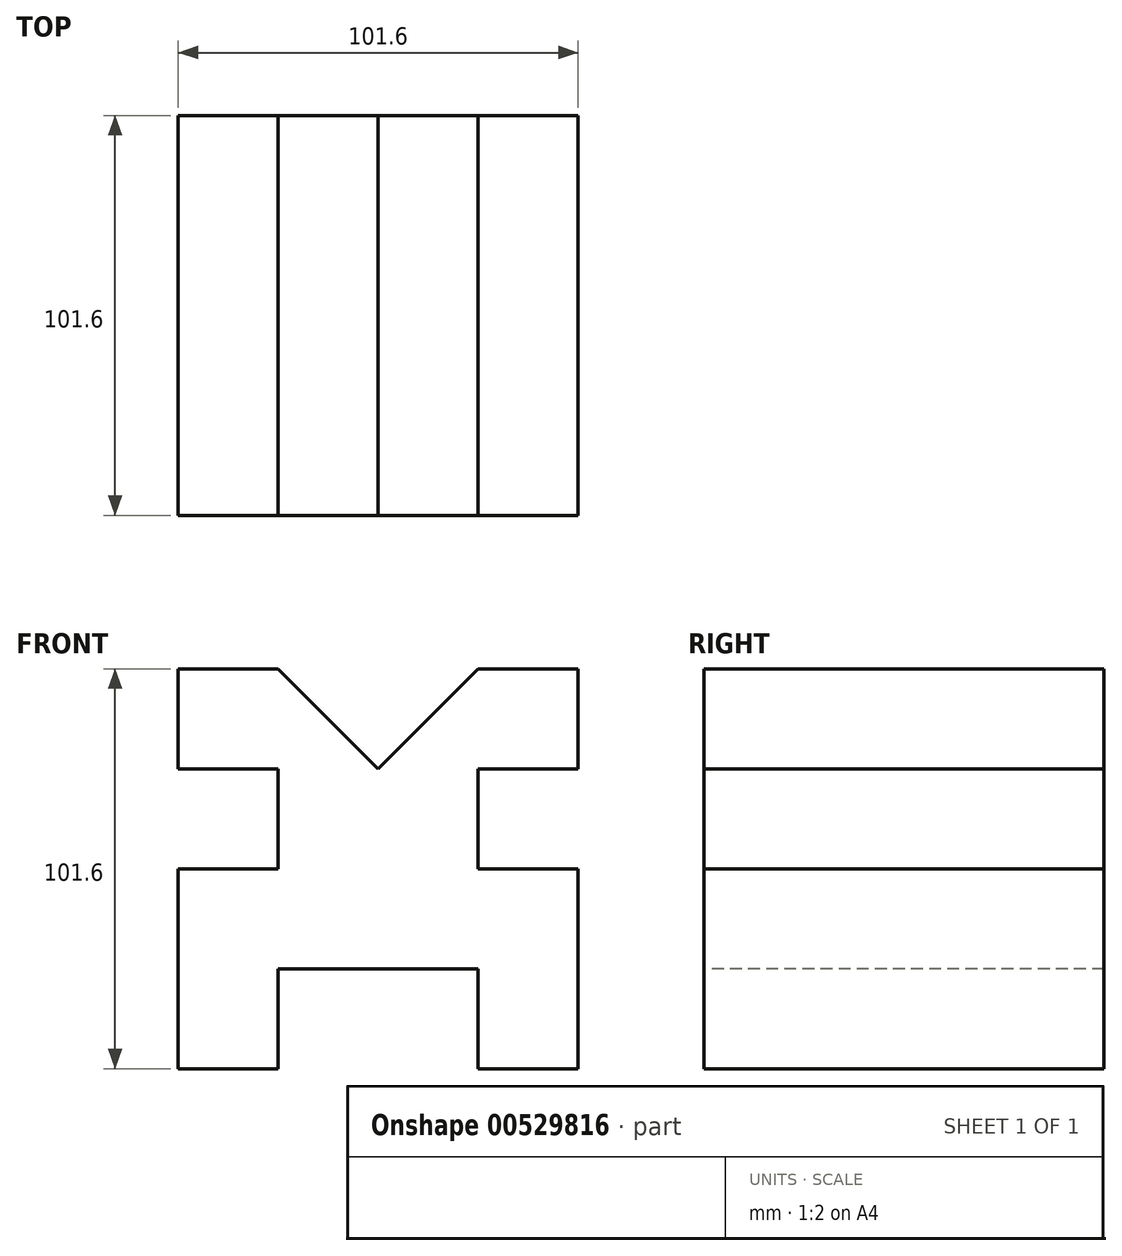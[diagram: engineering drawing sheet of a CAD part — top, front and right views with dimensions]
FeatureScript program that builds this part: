
annotation { "Feature Type Name" : "Feature", "Feature Type Description" : "" }
export const myFeature = defineFeature(function(context is Context, id is Id, definition is map)
    precondition{}
    {
        {
            var Q0;
            Q0=qCreatedBy(makeId("Front.planeOp"),FACE);
            var sketch = newSketch(context, id + "F0", { "sketchPlane" : qUnion([Q0])});
            skLineSegment(sketch, "E0.bottom", {"start": v(-154.32, -86.43) * mm, "end": v(-52.72, -86.43) * mm});
            skLineSegment(sketch, "E0.top", {"start": v(-154.32, 15.17) * mm, "end": v(-52.72, 15.17) * mm});
            skLineSegment(sketch, "E0.left", {"start": v(-154.32, -86.43) * mm, "end": v(-154.32, 15.17) * mm});
            skLineSegment(sketch, "E0.right", {"start": v(-52.72, -86.43) * mm, "end": v(-52.72, 15.17) * mm});
            skSolve(sketch);
        }
        {
            var Q0;
            Q0=makeQuery(id+"F0.imprint","IMPRINT",FACE,{"disambiguationData":[TD([[makeQuery(id+"F0.imprint","IMPRINT",EDGE,{"derivedFrom":sQuery(id+"F0.wireOp",EDGE,"E0.bottom")}),1.0]])]});
            extrude(context, id + "F1", {"entities" : qUnion([Q0]), "depth" : 101.6 * mm, "offsetDistance" : 25.4 * mm});
        }
        {
            var Q0;
            Q0=makeQuery(id+"F1.opExtrude","CAP_FACE",FACE,{"disambiguationData":[OSD([sQuery(id+"F0.wireOp",EDGE,"E0.bottom"),sQuery(id+"F0.wireOp",EDGE,"E0.top"),sQuery(id+"F0.wireOp",EDGE,"E0.left"),sQuery(id+"F0.wireOp",EDGE,"E0.right")])],"isStart":false});
            var sketch = newSketch(context, id + "F2", { "sketchPlane" : qUnion([Q0])});
            skLineSegment(sketch, "E1.bottom", {"start": v(-154.32, 15.17) * mm, "end": v(-128.92, 15.17) * mm});
            skLineSegment(sketch, "E1.top", {"start": v(-154.32, -10.23) * mm, "end": v(-128.92, -10.23) * mm});
            skLineSegment(sketch, "E1.left", {"start": v(-154.32, 15.17) * mm, "end": v(-154.32, -10.23) * mm});
            skLineSegment(sketch, "E1.right", {"start": v(-128.92, 15.17) * mm, "end": v(-128.92, -10.23) * mm});
            skLineSegment(sketch, "E2.bottom", {"start": v(-154.32, -86.43) * mm, "end": v(-128.92, -86.43) * mm});
            skLineSegment(sketch, "E2.top", {"start": v(-154.32, -35.63) * mm, "end": v(-128.92, -35.63) * mm});
            skLineSegment(sketch, "E2.left", {"start": v(-154.32, -86.43) * mm, "end": v(-154.32, -35.63) * mm});
            skLineSegment(sketch, "E2.right", {"start": v(-128.92, -86.43) * mm, "end": v(-128.92, -35.63) * mm});
            skLineSegment(sketch, "E3", {"start": v(-128.92, -35.63) * mm, "end": v(-128.92, -10.23) * mm});
            skLineSegment(sketch, "E4.bottom", {"start": v(-52.72, 15.17) * mm, "end": v(-78.12, 15.17) * mm});
            skLineSegment(sketch, "E4.top", {"start": v(-52.72, -10.23) * mm, "end": v(-78.12, -10.23) * mm});
            skLineSegment(sketch, "E4.left", {"start": v(-52.72, 15.17) * mm, "end": v(-52.72, -10.23) * mm});
            skLineSegment(sketch, "E4.right", {"start": v(-78.12, 15.17) * mm, "end": v(-78.12, -10.23) * mm});
            skLineSegment(sketch, "E5.bottom", {"start": v(-52.72, -86.43) * mm, "end": v(-78.12, -86.43) * mm});
            skLineSegment(sketch, "E5.top", {"start": v(-52.72, -35.63) * mm, "end": v(-78.12, -35.63) * mm});
            skLineSegment(sketch, "E5.left", {"start": v(-52.72, -86.43) * mm, "end": v(-52.72, -35.63) * mm});
            skLineSegment(sketch, "E5.right", {"start": v(-78.12, -86.43) * mm, "end": v(-78.12, -35.63) * mm});
            skLineSegment(sketch, "E6", {"start": v(-78.12, -10.23) * mm, "end": v(-78.12, -35.63) * mm});
            skSolve(sketch);
        }
        {
            var Q0;
            {var subQ0=sQuery(id+"F2.wireOp",EDGE,"E4.top");Q0=makeQuery(id+"F2.imprint","IMPRINT",FACE,{"disambiguationData":[TD([[makeQuery(id+"F2.imprint","IMPRINT",EDGE,{"derivedFrom":subQ0}),1.0]])]});}
            var Q1;
            {var subQ0=sQuery(id+"F2.wireOp",EDGE,"E1.top");Q1=makeQuery(id+"F2.imprint","IMPRINT",FACE,{"disambiguationData":[TD([[makeQuery(id+"F2.imprint","IMPRINT",EDGE,{"derivedFrom":subQ0}),-1.0]])]});}
            extrude(context, id + "F3", {"entities" : qUnion([Q0, Q1]), "operationType" : NewBodyOperationType.REMOVE, "oppositeDirection" : true, "depth" : 101.6 * mm, "offsetDistance" : 25.4 * mm});
        }
        {
            var Q0;
            Q0=makeQuery(id+"F1.opExtrude","CAP_FACE",FACE,{"disambiguationData":[OSD([sQuery(id+"F0.wireOp",EDGE,"E0.bottom"),sQuery(id+"F0.wireOp",EDGE,"E0.top"),sQuery(id+"F0.wireOp",EDGE,"E0.left"),sQuery(id+"F0.wireOp",EDGE,"E0.right")])],"isStart":false});
            var sketch = newSketch(context, id + "F4", { "sketchPlane" : qUnion([Q0])});
            skLineSegment(sketch, "E7", {"start": v(-128.92, -10.23) * mm, "end": v(-78.12, -10.23) * mm});
            skLineSegment(sketch, "E8", {"start": v(-128.92, 15.17) * mm, "end": v(-103.52, -10.23) * mm});
            skLineSegment(sketch, "E9", {"start": v(-78.12, 15.17) * mm, "end": v(-103.52, -10.23) * mm});
            skSolve(sketch);
        }
        {
            var Q0;
            {var subQ0=sQuery(id+"F4.wireOp",EDGE,"E8");Q0=makeQuery(id+"F4.imprint","IMPRINT",FACE,{"disambiguationData":[TD([[makeQuery(id+"F4.imprint","IMPRINT",EDGE,{"derivedFrom":subQ0}),1.0]])]});}
            extrude(context, id + "F5", {"entities" : qUnion([Q0]), "operationType" : NewBodyOperationType.REMOVE, "oppositeDirection" : true, "depth" : 101.6 * mm, "offsetDistance" : 25.4 * mm});
        }
        {
            var Q0;
            Q0=makeQuery(id+"F1.opExtrude","CAP_FACE",FACE,{"disambiguationData":[OSD([sQuery(id+"F0.wireOp",EDGE,"E0.bottom"),sQuery(id+"F0.wireOp",EDGE,"E0.top"),sQuery(id+"F0.wireOp",EDGE,"E0.left"),sQuery(id+"F0.wireOp",EDGE,"E0.right")])],"isStart":false});
            var sketch = newSketch(context, id + "F6", { "sketchPlane" : qUnion([Q0])});
            skLineSegment(sketch, "E10.bottom", {"start": v(-154.32, -86.43) * mm, "end": v(-128.92, -86.43) * mm});
            skLineSegment(sketch, "E10.top", {"start": v(-154.32, -61.03) * mm, "end": v(-128.92, -61.03) * mm});
            skLineSegment(sketch, "E10.left", {"start": v(-154.32, -86.43) * mm, "end": v(-154.32, -61.03) * mm});
            skLineSegment(sketch, "E10.right", {"start": v(-128.92, -86.43) * mm, "end": v(-128.92, -61.03) * mm});
            skLineSegment(sketch, "E11.bottom", {"start": v(-52.72, -86.43) * mm, "end": v(-78.12, -86.43) * mm});
            skLineSegment(sketch, "E11.top", {"start": v(-52.72, -61.03) * mm, "end": v(-78.12, -61.03) * mm});
            skLineSegment(sketch, "E11.left", {"start": v(-52.72, -86.43) * mm, "end": v(-52.72, -61.03) * mm});
            skLineSegment(sketch, "E11.right", {"start": v(-78.12, -86.43) * mm, "end": v(-78.12, -61.03) * mm});
            skLineSegment(sketch, "E12", {"start": v(-128.92, -61.03) * mm, "end": v(-78.12, -61.03) * mm});
            skSolve(sketch);
        }
        {
            var Q0;
            {var subQ0=sQuery(id+"F6.wireOp",EDGE,"E10.right");Q0=makeQuery(id+"F6.imprint","IMPRINT",FACE,{"disambiguationData":[TD([[makeQuery(id+"F6.imprint","IMPRINT",EDGE,{"derivedFrom":subQ0}),-1.0]])]});}
            extrude(context, id + "F7", {"entities" : qUnion([Q0]), "operationType" : NewBodyOperationType.REMOVE, "oppositeDirection" : true, "depth" : 101.6 * mm, "offsetDistance" : 25.4 * mm});
        }
    });
